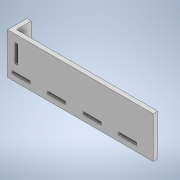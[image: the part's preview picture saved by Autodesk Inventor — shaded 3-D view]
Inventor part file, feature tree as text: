
AUTODESK INVENTOR PART (.ipt)
format: ipt  version: 2022 (Build 260153000, 153)  size: 154,624 bytes
history: native  units: mm
features: extrude x4, sketch x3
ambient origin geometry x8: Origin, YZ Plane, XZ Plane, XY Plane, X Axis, Y Axis, Z Axis, Center Point
bodies: Solid1 (feature_tree)
feature tree (7):
  sketch  "Sketch1"  dims[d0=198.085mm d1=56.25mm]
  extrude  "Extrusion1"  Depth=56.25mm
  extrude  "Extrusion2"  TaperAngle=0.0deg  [1 undecoded]
  extrude  "Extrusion3"  Depth=6.085mm
  extrude  "Extrusion4"  Depth=4.17mm
  sketch  "Sketch2"  dims[d2=0.0mm d3=0.0mm]
  sketch  "Sketch3"  dims[d4=0.0mm d5=6.085mm d6=4.17mm d7=10.15mm d8=3.7mm d9=24.4mm d10=7.75mm d11=0.0mm d12=24.75mm d13=40.0mm d15=48.31mm d16=10.0mm d18=10.0mm d20=3.5mm d21=6.085mm d22=0.0mm d23=26.125mm d24=0.0mm d25=84.0mm d26=37.0mm d27=20.75mm d28=26.125mm d29=0.0mm d30=13.5mm d31=11.25mm d32=10.0mm d33=0.0mm]
note: 1 required parameter value undecoded (feature->parameter linkage not recoverable at this tier; creation-order binding heuristic only, values carry confidence <= 0.55)
